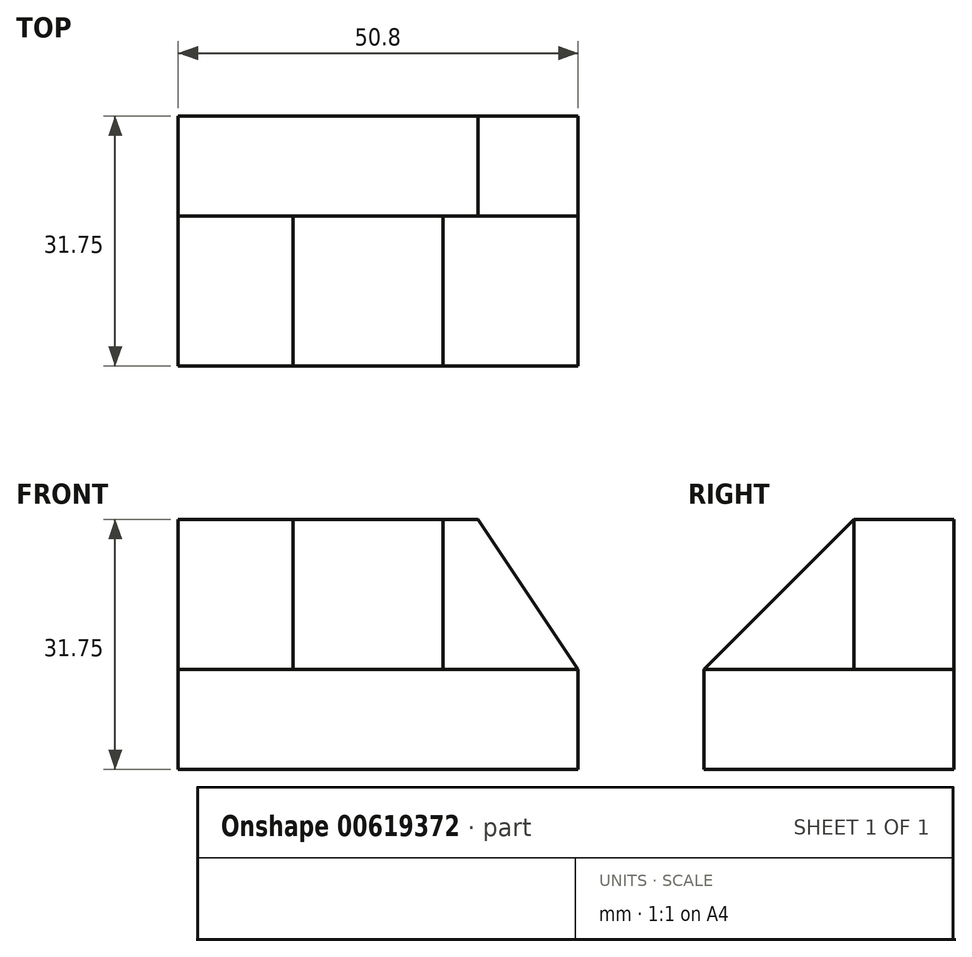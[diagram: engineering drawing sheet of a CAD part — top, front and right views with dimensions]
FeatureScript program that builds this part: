
annotation { "Feature Type Name" : "Feature", "Feature Type Description" : "" }
export const myFeature = defineFeature(function(context is Context, id is Id, definition is map)
    precondition{}
    {
        {
            var Q0;
            Q0=qCreatedBy(makeId("Right.planeOp"),FACE);
            var sketch = newSketch(context, id + "F0", { "sketchPlane" : qUnion([Q0])});
            skLineSegment(sketch, "E0", {"start": v(0, 0) * mm, "end": v(31.75, 0) * mm});
            skLineSegment(sketch, "E1", {"start": v(31.75, 0) * mm, "end": v(31.75, 12.7) * mm});
            skLineSegment(sketch, "E2", {"start": v(31.75, 12.7) * mm, "end": v(0, 12.7) * mm});
            skLineSegment(sketch, "E3", {"start": v(0, 12.7) * mm, "end": v(0, 0) * mm});
            skSolve(sketch);
        }
        {
            var Q0;
            Q0 = qSketchRegion(id + "F0", true);
            extrude(context, id + "F1", {"entities" : qUnion([Q0]), "depth" : 50.8 * mm, "offsetDistance" : 25.4 * mm});
        }
        {
            var Q0;
            Q0=makeQuery(id+"F1.opExtrude","SWEPT_FACE",FACE,{"disambiguationData":[OSD([sQuery(id+"F0.wireOp",EDGE,"E1")])]});
            var sketch = newSketch(context, id + "F2", { "sketchPlane" : qUnion([Q0])});
            skLineSegment(sketch, "E4", {"start": v(0, 12.7) * mm, "end": v(0, 31.75) * mm});
            skLineSegment(sketch, "E5", {"start": v(0, 31.75) * mm, "end": v(-50.8, 31.75) * mm});
            skLineSegment(sketch, "E6", {"start": v(-50.8, 31.75) * mm, "end": v(-50.8, 12.7) * mm});
            skLineSegment(sketch, "E7", {"start": v(-50.8, 12.7) * mm, "end": v(0, 12.7) * mm});
            skSolve(sketch);
        }
        {
            var Q0;
            Q0 = qSketchRegion(id + "F2", true);
            extrude(context, id + "F3", {"entities" : qUnion([Q0]), "oppositeDirection" : true, "depth" : 12.7 * mm, "offsetDistance" : 25.4 * mm});
        }
        {
            var Q0;
            Q0=makeQuery(id+"F3.opExtrude","CAP_FACE",FACE,{"disambiguationData":[OSD([sQuery(id+"F2.wireOp",EDGE,"E4"),sQuery(id+"F2.wireOp",EDGE,"E5"),sQuery(id+"F2.wireOp",EDGE,"E6"),sQuery(id+"F2.wireOp",EDGE,"E7")])],"isStart":false});
            var sketch = newSketch(context, id + "F4", { "sketchPlane" : qUnion([Q0])});
            skLineSegment(sketch, "E8", {"start": v(38.1, 31.75) * mm, "end": v(50.8, 12.7) * mm});
            skSolve(sketch);
        }
        {
            var Q0;
            {var subQ0=sQuery(id+"F4.wireOp",EDGE,"E8");Q0=makeQuery(id+"F4.imprint","IMPRINT",FACE,{"disambiguationData":[TD([[makeQuery(id+"F4.imprint","IMPRINT",EDGE,{"derivedFrom":subQ0}),1.0]])]});}
            extrude(context, id + "F5", {"entities" : qUnion([Q0]), "operationType" : NewBodyOperationType.REMOVE, "oppositeDirection" : true, "depth" : 25.4 * mm, "offsetDistance" : 25.4 * mm});
        }
        {
            var Q0;
            Q0=makeQuery(id+"F1.opExtrude","SWEPT_FACE",FACE,{"disambiguationData":[OSD([sQuery(id+"F0.wireOp",EDGE,"E2")])]});
            var sketch = newSketch(context, id + "F6", { "sketchPlane" : qUnion([Q0])});
            skLineSegment(sketch, "E9", {"start": v(14.61, 19.05) * mm, "end": v(14.61, 0) * mm});
            skLineSegment(sketch, "E10", {"start": v(33.66, 19.05) * mm, "end": v(33.66, 0) * mm});
            skLineSegment(sketch, "E11", {"start": v(14.61, 0) * mm, "end": v(33.66, 0) * mm});
            skLineSegment(sketch, "E12", {"start": v(33.66, 19.05) * mm, "end": v(14.61, 19.05) * mm});
            skSolve(sketch);
        }
        {
            var Q0;
            Q0 = qSketchRegion(id + "F6", true);
            extrude(context, id + "F7", {"entities" : qUnion([Q0]), "depth" : 19.05 * mm, "offsetDistance" : 25.4 * mm});
        }
        {
            var Q0;
            Q0=makeQuery(id+"F7.opExtrude","SWEPT_FACE",FACE,{"disambiguationData":[OSD([sQuery(id+"F6.wireOp",EDGE,"E10")])]});
            var sketch = newSketch(context, id + "F8", { "sketchPlane" : qUnion([Q0])});
            skLineSegment(sketch, "E13", {"start": v(19.05, 31.75) * mm, "end": v(0, 12.7) * mm});
            skSolve(sketch);
        }
        {
            var Q0;
            Q0=makeQuery(id+"F8.imprint","IMPRINT",FACE,{"disambiguationData":[TD([[makeQuery(id+"F8.imprint","IMPRINT",EDGE,{"derivedFrom":sQuery(id+"F8.wireOp",EDGE,"E13")}),-1.0]])]});
            extrude(context, id + "F9", {"entities" : qUnion([Q0]), "operationType" : NewBodyOperationType.REMOVE, "oppositeDirection" : true, "depth" : 25.4 * mm, "offsetDistance" : 25.4 * mm});
        }
    });
